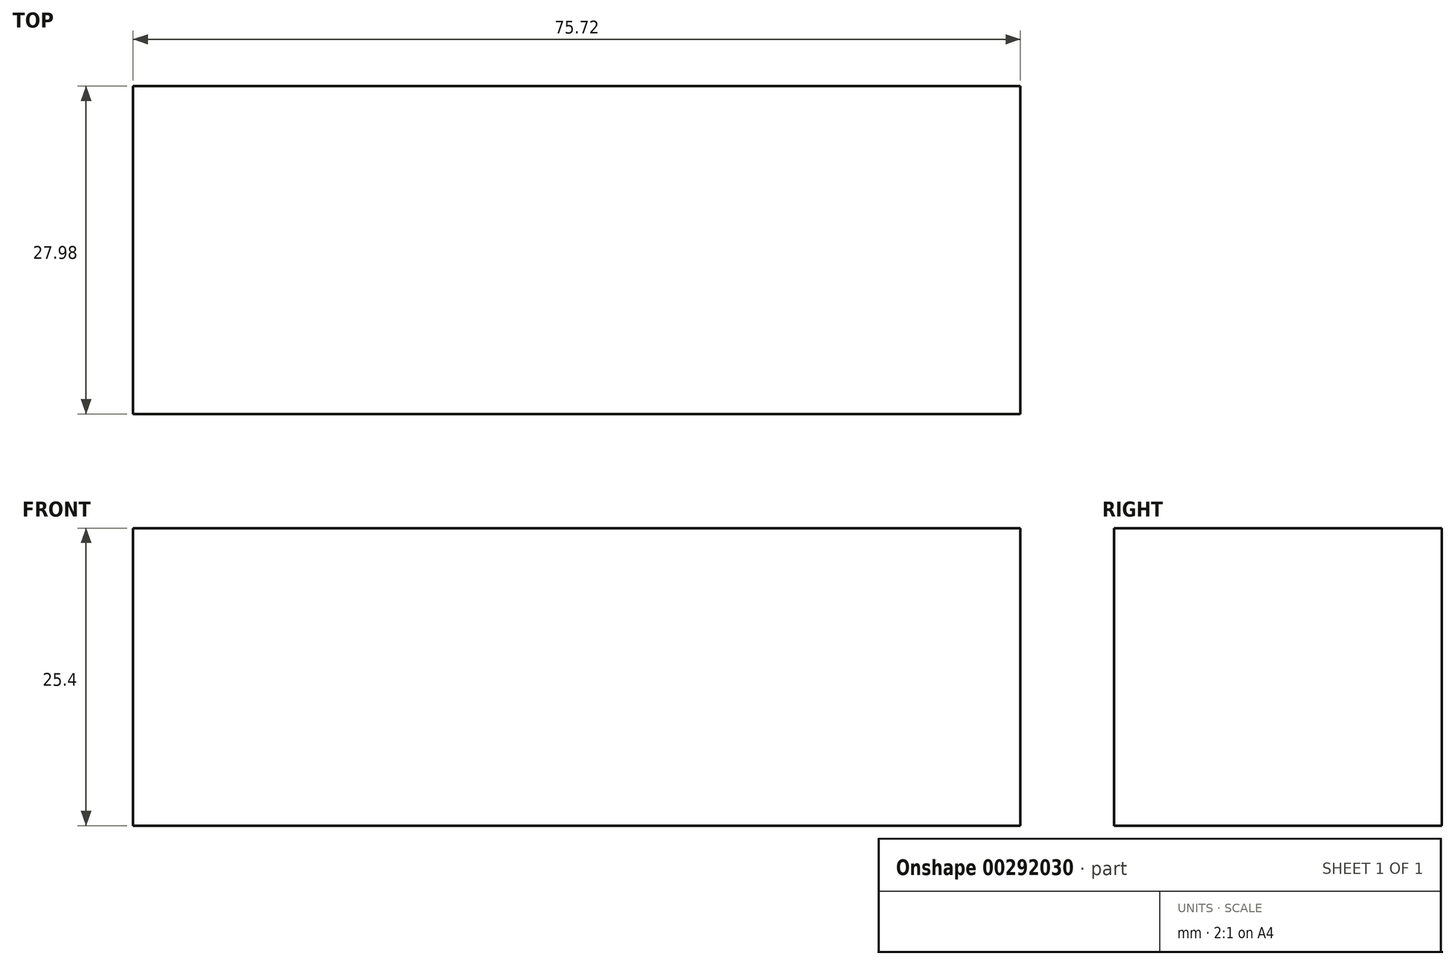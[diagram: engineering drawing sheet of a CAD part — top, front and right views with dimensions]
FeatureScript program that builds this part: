
annotation { "Feature Type Name" : "Feature", "Feature Type Description" : "" }
export const myFeature = defineFeature(function(context is Context, id is Id, definition is map)
    precondition{}
    {
        {
            var Q0;
            Q0=qCreatedBy(makeId("Top.planeOp"),FACE);
            var sketch = newSketch(context, id + "F0", { "sketchPlane" : qUnion([Q0])});
            skLineSegment(sketch, "E0.bottom", {"start": v(9.93, 44.89) * mm, "end": v(85.65, 44.89) * mm});
            skLineSegment(sketch, "E0.top", {"start": v(9.93, 16.9) * mm, "end": v(85.65, 16.9) * mm});
            skLineSegment(sketch, "E0.left", {"start": v(9.93, 44.89) * mm, "end": v(9.93, 16.9) * mm});
            skLineSegment(sketch, "E0.right", {"start": v(85.65, 44.89) * mm, "end": v(85.65, 16.9) * mm});
            skSolve(sketch);
        }
        {
            var Q0;
            Q0=makeQuery(id+"F0.imprint","IMPRINT",FACE,{"disambiguationData":[TD([[makeQuery(id+"F0.imprint","IMPRINT",EDGE,{"derivedFrom":sQuery(id+"F0.wireOp",EDGE,"E0.bottom")}),-1.0]])]});
            extrude(context, id + "F1", {"entities" : qUnion([Q0]), "depth" : 25.4 * mm});
        }
    });
